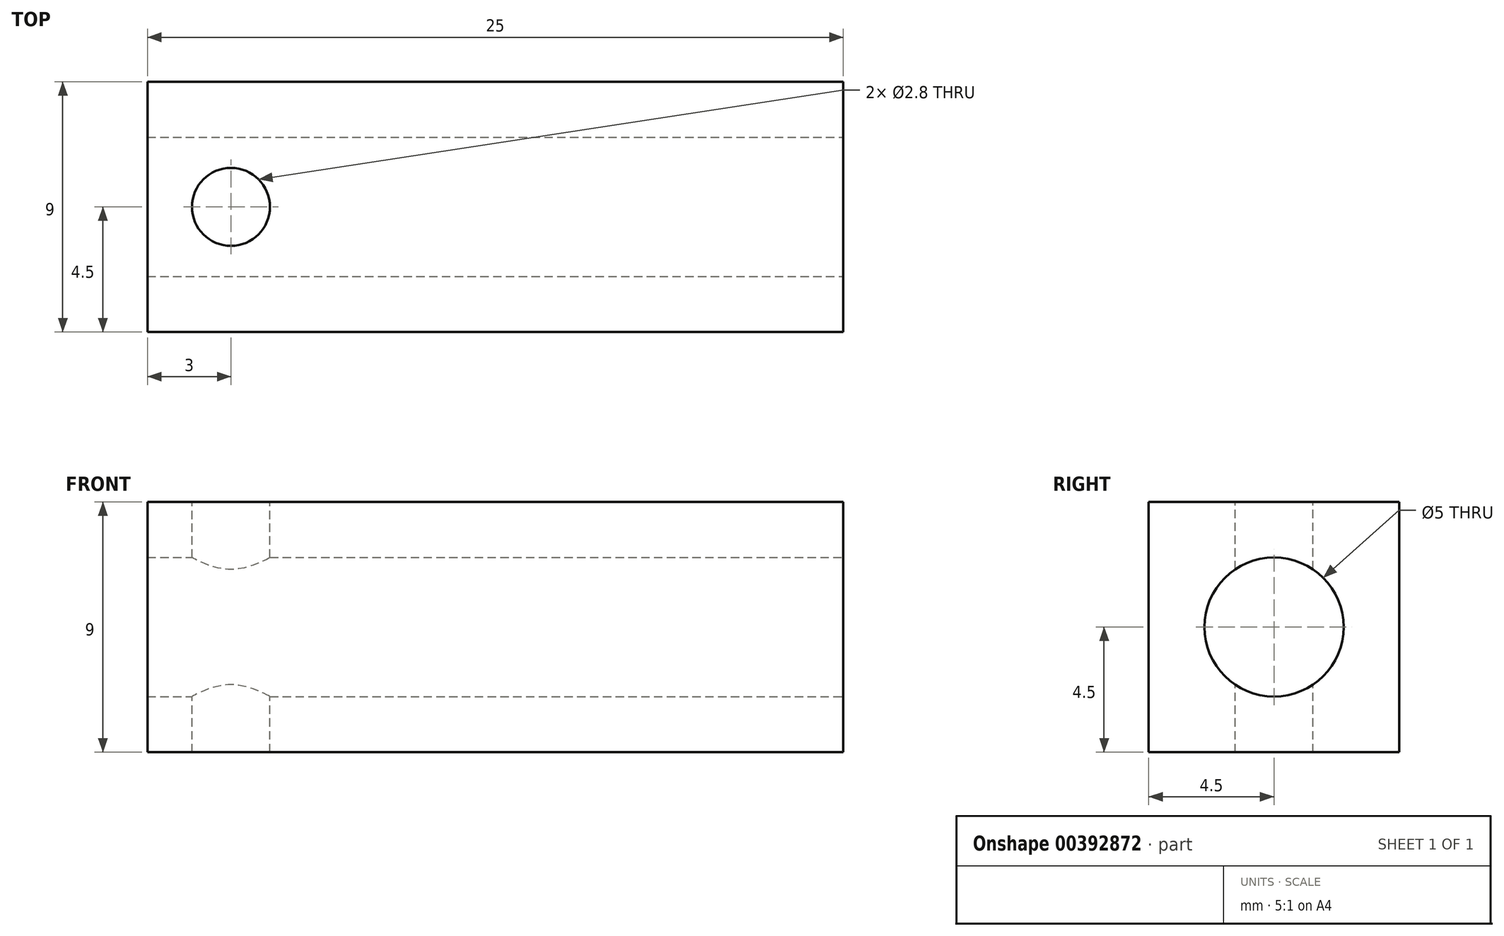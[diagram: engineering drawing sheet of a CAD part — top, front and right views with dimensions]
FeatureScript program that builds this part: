
annotation { "Feature Type Name" : "Feature", "Feature Type Description" : "" }
export const myFeature = defineFeature(function(context is Context, id is Id, definition is map)
    precondition{}
    {
        {
            var Q0;
            Q0=qCreatedBy(makeId("Top.planeOp"),FACE);
            var sketch = newSketch(context, id + "F0", { "sketchPlane" : qUnion([Q0])});
            skLineSegment(sketch, "E0.bottom", {"start": v(10, -4.5) * mm, "end": v(-15, -4.5) * mm});
            skLineSegment(sketch, "E0.top", {"start": v(10, 4.5) * mm, "end": v(-15, 4.5) * mm});
            skLineSegment(sketch, "E0.left", {"start": v(10, -4.5) * mm, "end": v(10, 4.5) * mm});
            skLineSegment(sketch, "E0.right", {"start": v(-15, -4.5) * mm, "end": v(-15, 4.5) * mm});
            skLineSegment(sketch, "E1", {"start": v(0, 0) * mm, "end": v(10, 0) * mm});
            skLineSegment(sketch, "E2.bottom", {"start": v(-5, -4.5) * mm, "end": v(-15, -4.5) * mm});
            skLineSegment(sketch, "E2.right", {"start": v(-15, -4.5) * mm, "end": v(-15, -2.5) * mm});
            skSolve(sketch);
        }
        {
            var Q0;
            {var subQ3=sQuery(id+"F0.wireOp",EDGE,"E0.bottom");Q0=makeQuery(id+"F0.imprint","IMPRINT",FACE,{"disambiguationData":[TD([[makeQuery(id+"F0.imprint","IMPRINT",EDGE,{"derivedFrom":subQ3}),-1.0]])]});}
            extrude(context, id + "F1", {"entities" : qUnion([Q0]), "depth" : 9 * mm});
        }
        {
            var Q0;
            Q0=makeQuery(id+"F1.opExtrude","SWEPT_FACE",FACE,{"disambiguationData":[OSD([sQuery(id+"F0.wireOp",EDGE,"E0.left")])]});
            var sketch = newSketch(context, id + "F2", { "sketchPlane" : qUnion([Q0])});
            skCircle(sketch, "E3", {"center": v(0, 4.5) * mm, "radius": 2.5 * mm});
            skPoint(sketch, "E3.centerSnap0", {"position": v(4.5, 4.5) * mm});
            skSolve(sketch);
        }
        {
            var Q0;
            Q0=makeQuery(id+"F1.opExtrude","CAP_FACE",FACE,{"disambiguationData":[OSD([sQuery(id+"F0.wireOp",EDGE,"E0.bottom"),sQuery(id+"F0.wireOp",EDGE,"E0.top"),sQuery(id+"F0.wireOp",EDGE,"E0.left"),sQuery(id+"F0.wireOp",EDGE,"E0.right"),sQuery(id+"F0.wireOp",EDGE,"E2.bottom"),sQuery(id+"F0.wireOp",EDGE,"E2.right")])],"isStart":false});
            var sketch = newSketch(context, id + "F3", { "sketchPlane" : qUnion([Q0])});
            skCircle(sketch, "E4", {"center": v(-12, 0) * mm, "radius": 1.4 * mm});
            skPoint(sketch, "E4.centerSnap0", {"position": v(-15, 0) * mm});
            skSolve(sketch);
        }
        {
            var Q0;
            Q0=makeQuery(id+"F3.imprint","IMPRINT",FACE,{"disambiguationData":[TD([[makeQuery(id+"F3.imprint","IMPRINT",EDGE,{"derivedFrom":sQuery(id+"F3.wireOp",EDGE,"E4")}),1.0]])]});
            extrude(context, id + "F4", {"entities" : qUnion([Q0]), "operationType" : NewBodyOperationType.REMOVE, "oppositeDirection" : true, "depth" : 25 * mm});
        }
        {
            var Q0;
            Q0=makeQuery(id+"F2.imprint","IMPRINT",FACE,{"disambiguationData":[TD([[makeQuery(id+"F2.imprint","IMPRINT",EDGE,{"derivedFrom":sQuery(id+"F2.wireOp",EDGE,"E3")}),1.0]])]});
            extrude(context, id + "F5", {"entities" : qUnion([Q0]), "operationType" : NewBodyOperationType.REMOVE, "oppositeDirection" : true, "depth" : 25 * mm});
        }
    });
